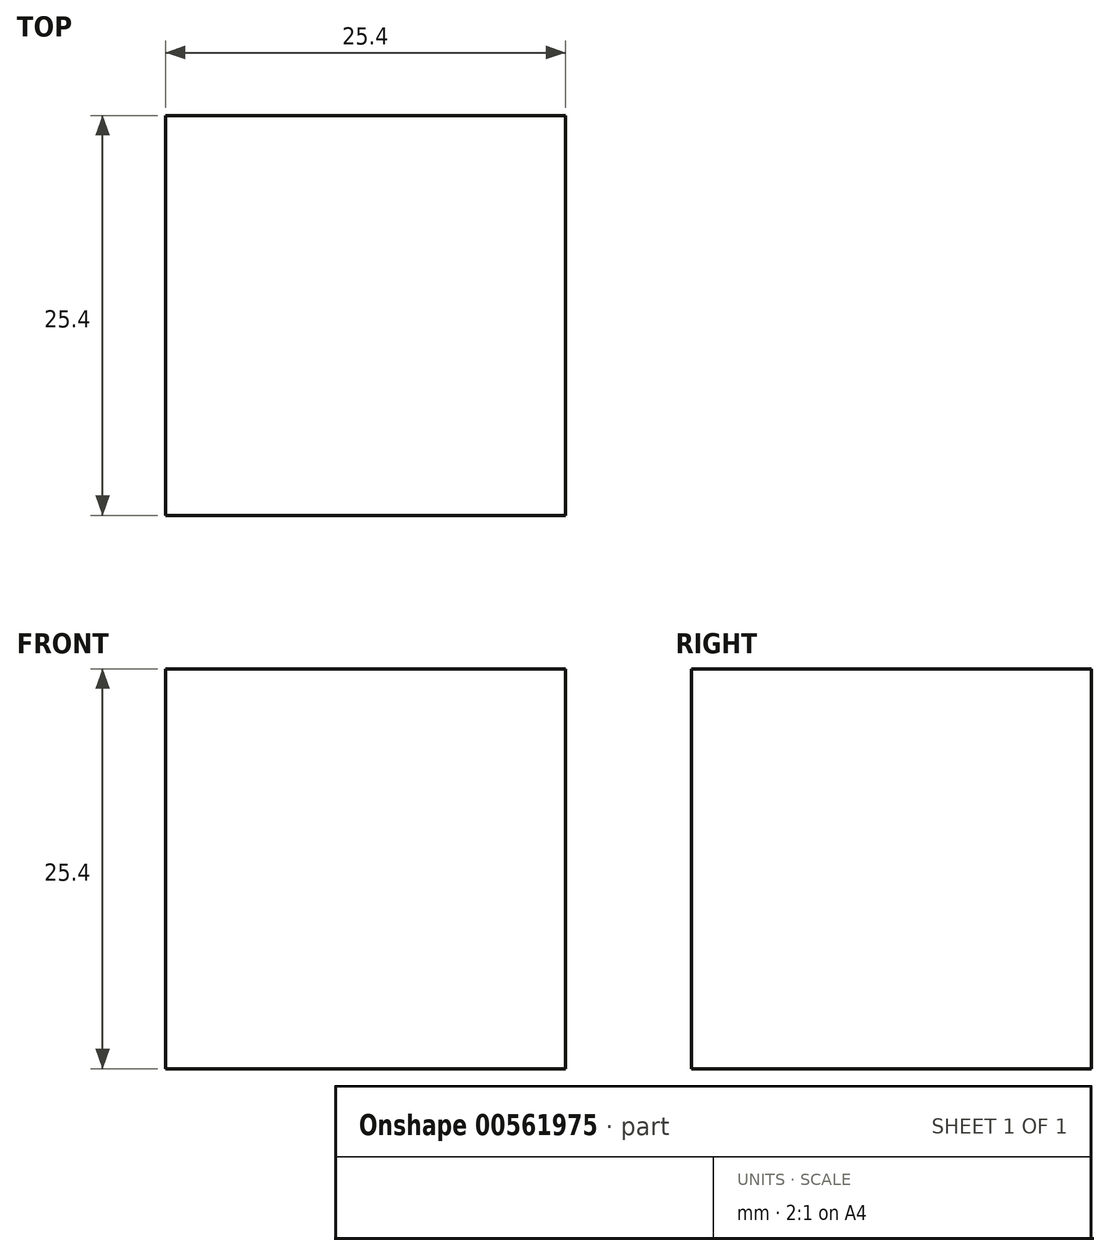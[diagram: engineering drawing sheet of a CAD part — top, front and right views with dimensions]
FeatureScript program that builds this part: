
annotation { "Feature Type Name" : "Feature", "Feature Type Description" : "" }
export const myFeature = defineFeature(function(context is Context, id is Id, definition is map)
    precondition{}
    {
        {
            var Q0;
            Q0=qCreatedBy(makeId("Front.planeOp"),FACE);
            var sketch = newSketch(context, id + "F0", { "sketchPlane" : qUnion([Q0])});
            skLineSegment(sketch, "E0.bottom", {"start": v(-61.04, 56.9) * mm, "end": v(-35.64, 56.9) * mm});
            skLineSegment(sketch, "E0.top", {"start": v(-61.04, 31.5) * mm, "end": v(-35.64, 31.5) * mm});
            skLineSegment(sketch, "E0.left", {"start": v(-61.04, 56.9) * mm, "end": v(-61.04, 31.5) * mm});
            skLineSegment(sketch, "E0.right", {"start": v(-35.64, 56.9) * mm, "end": v(-35.64, 31.5) * mm});
            skSolve(sketch);
        }
        {
            var Q0;
            Q0=makeQuery(id+"F0.imprint","IMPRINT",FACE,{"disambiguationData":[TD([[makeQuery(id+"F0.imprint","IMPRINT",EDGE,{"derivedFrom":sQuery(id+"F0.wireOp",EDGE,"E0.bottom")}),-1.0]])]});
            extrude(context, id + "F1", {"entities" : qUnion([Q0]), "depth" : 25.4 * mm, "offsetDistance" : 25.4 * mm});
        }
    });
